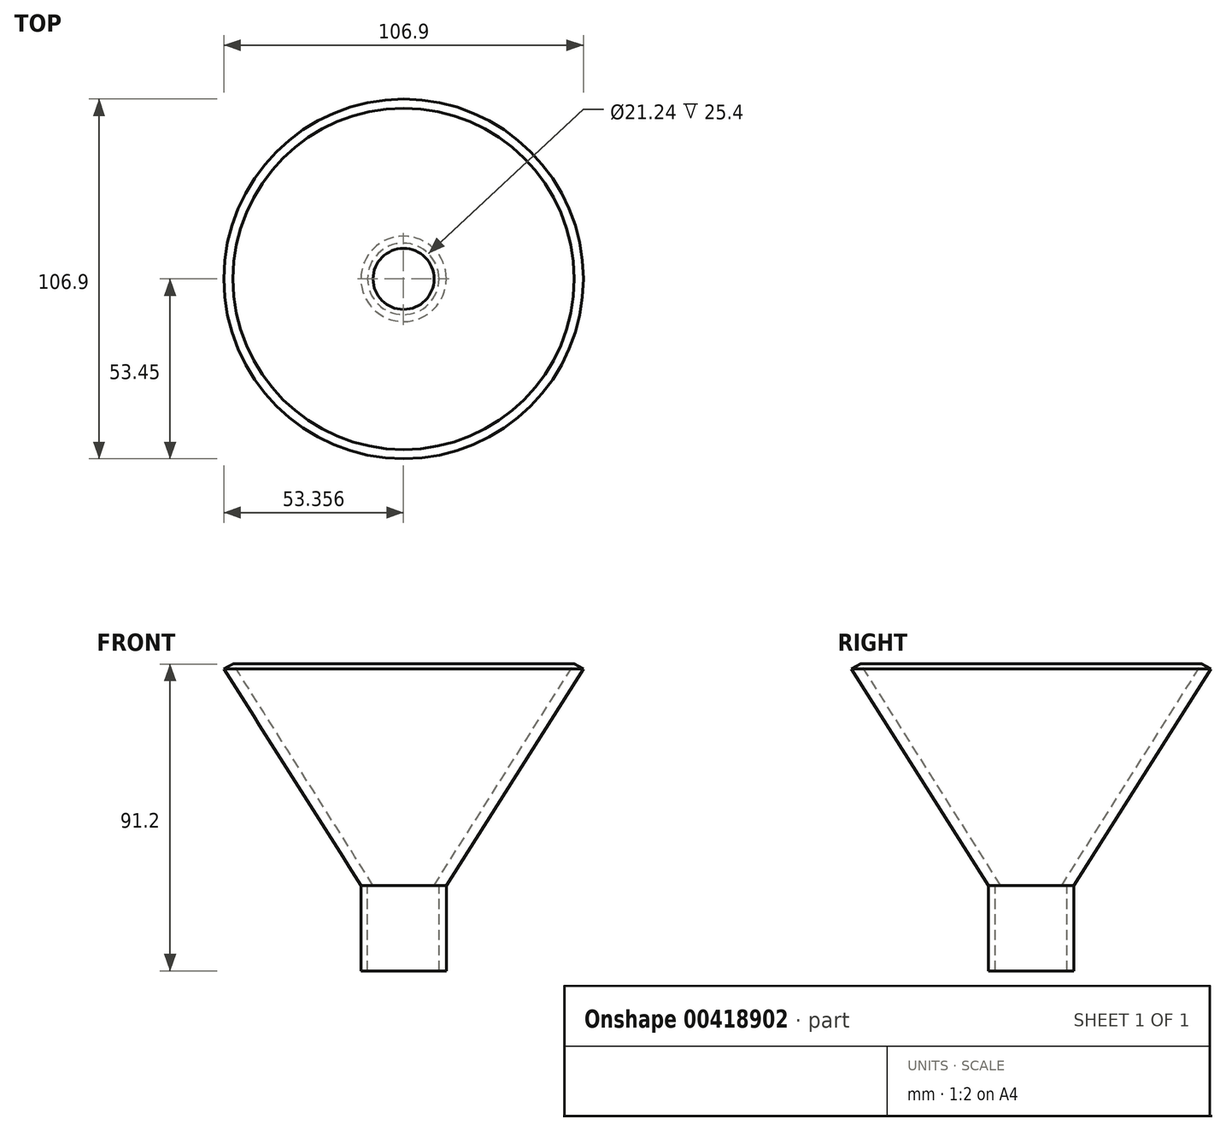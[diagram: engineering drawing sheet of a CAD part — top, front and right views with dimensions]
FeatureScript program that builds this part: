
annotation { "Feature Type Name" : "Feature", "Feature Type Description" : "" }
export const myFeature = defineFeature(function(context is Context, id is Id, definition is map)
    precondition{}
    {
        {
            var Q0;
            Q0=qCreatedBy(makeId("Front.planeOp"),FACE);
            var sketch = newSketch(context, id + "F0", { "sketchPlane" : qUnion([Q0])});
            skLineSegment(sketch, "E0", {"start": v(0, 0) * mm, "end": v(40.75, 64.4) * mm});
            skLineSegment(sketch, "E1", {"start": v(0, 0) * mm, "end": v(0, -25.4) * mm});
            skLineSegment(sketch, "E2", {"start": v(0, -25.4) * mm, "end": v(-12.7, -25.4) * mm});
            skLineSegment(sketch, "E3", {"start": v(-12.7, -25.4) * mm, "end": v(-12.7, 0) * mm});
            skLineSegment(sketch, "E4", {"start": v(-12.7, 0) * mm, "end": v(-3.63, 0) * mm});
            skLineSegment(sketch, "E5", {"start": v(-3.63, 0) * mm, "end": v(38, 65.8) * mm});
            skLineSegment(sketch, "E6", {"start": v(38, 65.8) * mm, "end": v(40.75, 64.4) * mm});
            skSolve(sketch);
        }
        {
            var Q0;
            Q0=makeQuery(id+"F0.imprint","IMPRINT",FACE,{"disambiguationData":[TD([[makeQuery(id+"F0.imprint","IMPRINT",EDGE,{"derivedFrom":sQuery(id+"F0.wireOp",EDGE,"E0")}),1.0]])]});
            var Q1;
            Q1=sQuery(id+"F0.wireOp",EDGE,"E3");
            revolve(context, id + "F1", {"entities" : qUnion([Q0]), "axis" : qUnion([Q1]), "revolveType" : RevolveType.FULL});
        }
        {
            var Q0;
            Q0=qCreatedBy(makeId("Top.planeOp"),FACE);
            var sketch = newSketch(context, id + "F2", { "sketchPlane" : qUnion([Q0])});
            skCircle(sketch, "E7", {"center": v(-12.8, 0) * mm, "radius": 10.62 * mm});
            skSolve(sketch);
        }
        {
            var Q0;
            Q0 = qSketchRegion(id + "F2", true);
            extrude(context, id + "F3", {"entities" : qUnion([Q0]), "operationType" : NewBodyOperationType.REMOVE, "oppositeDirection" : true, "depth" : 25.4 * mm});
        }
    });
